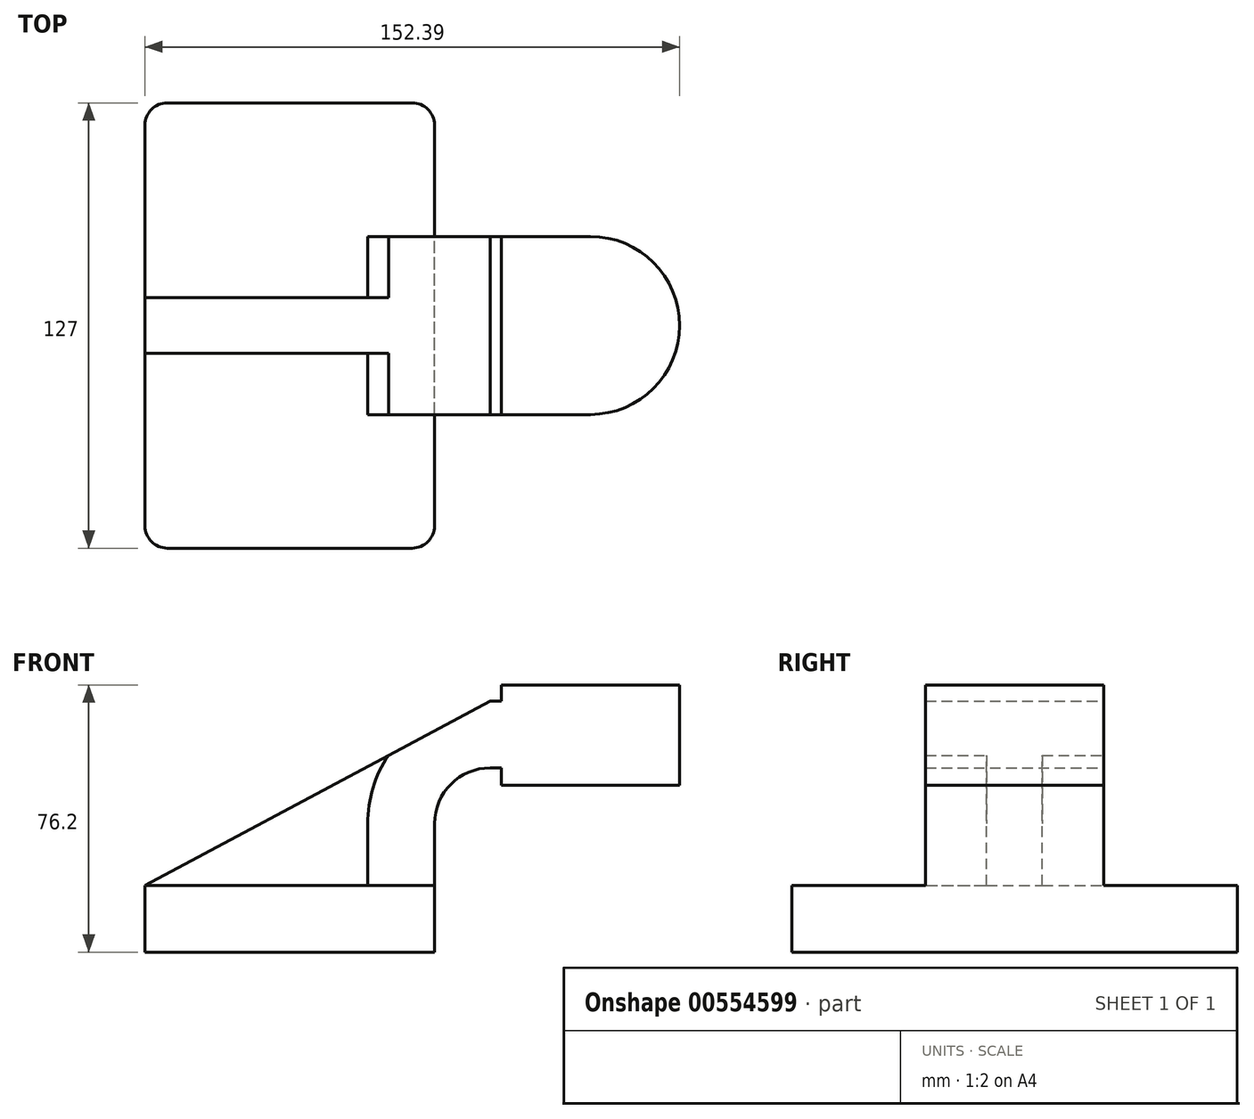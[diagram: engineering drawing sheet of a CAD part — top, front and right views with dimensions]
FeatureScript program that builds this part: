
annotation { "Feature Type Name" : "Feature", "Feature Type Description" : "" }
export const myFeature = defineFeature(function(context is Context, id is Id, definition is map)
    precondition{}
    {
        {
            var Q0;
            Q0=qCreatedBy(makeId("Front.planeOp"),FACE);
            var sketch = newSketch(context, id + "F0", { "sketchPlane" : qUnion([Q0])});
            skLineSegment(sketch, "E0.bottom", {"start": v(-41.28, 9.52) * mm, "end": v(41.27, 9.53) * mm});
            skLineSegment(sketch, "E0.top", {"start": v(-41.28, -9.53) * mm, "end": v(41.28, -9.53) * mm});
            skLineSegment(sketch, "E0.left", {"start": v(-41.28, 9.52) * mm, "end": v(-41.27, -9.53) * mm});
            skLineSegment(sketch, "E0.right", {"start": v(41.28, 9.53) * mm, "end": v(41.28, -9.52) * mm});
            skPoint(sketch, "E0.middle", {"position": v(0, 0) * mm});
            skLineSegment(sketch, "E1.bottom", {"start": v(60.32, 66.67) * mm, "end": v(111.12, 66.67) * mm});
            skLineSegment(sketch, "E1.top", {"start": v(60.33, 38.1) * mm, "end": v(111.12, 38.1) * mm});
            skLineSegment(sketch, "E1.left", {"start": v(60.32, 66.67) * mm, "end": v(60.33, 38.1) * mm});
            skLineSegment(sketch, "E1.right", {"start": v(111.12, 66.67) * mm, "end": v(111.12, 38.1) * mm});
            skPoint(sketch, "E1.middle", {"position": v(85.72, 52.39) * mm});
            skLineSegment(sketch, "E2", {"start": v(41.27, 9.53) * mm, "end": v(41.27, 27.13) * mm});
            skArc(sketch, "E3", {"start": v(41.27, 27.13) * mm, "mid": v(45.92, 38.35) * mm, "end": v(57.15, 43) * mm});
            skLineSegment(sketch, "E4", {"start": v(57.15, 43) * mm, "end": v(76.83, 43) * mm});
            skLineSegment(sketch, "E5.0", {"start": v(57.15, 62.05) * mm, "end": v(76.83, 62.05) * mm});
            skArc(sketch, "E5.1", {"start": v(22.22, 27.13) * mm, "mid": v(32.45, 51.82) * mm, "end": v(57.15, 62.05) * mm});
            skLineSegment(sketch, "E5.2", {"start": v(22.22, 9.53) * mm, "end": v(22.22, 27.13) * mm});
            skLineSegment(sketch, "E6", {"start": v(85.72, 38.1) * mm, "end": v(85.72, 66.67) * mm});
            skFitSpline(sketch, "E7", {"points": [v(-41.28, 9.52) * mm, v(57.15, 62.05) * mm], "startDerivative": vector(98.43, 52.53) * mm, "endDerivative": vector(98.43, 52.53) * mm});
            skSolve(sketch);
        }
        {
            var Q0;
            Q0=makeQuery(id+"F0.imprint","IMPRINT",FACE,{"disambiguationData":[TD([[makeQuery(id+"F0.imprint","IMPRINT",EDGE,{"derivedFrom":sQuery(id+"F0.wireOp",EDGE,"E0.top")}),1.0]])]});
            extrude(context, id + "F1", {"entities" : qUnion([Q0]), "endBound" : BoundingType.SYMMETRIC, "depth" : 127 * mm, "offsetDistance" : 25.4 * mm});
        }
        {
            var Q0;
            {var subQ1=sQuery(id+"F0.wireOp",EDGE,"E2");Q0=makeQuery(id+"F0.imprint","IMPRINT",FACE,{"disambiguationData":[TD([[makeQuery(id+"F0.imprint","IMPRINT",EDGE,{"derivedFrom":subQ1}),1.0]])]});}
            var Q1;
            {var subQ4=sQuery(id+"F0.wireOp",EDGE,"E6");Q1=makeQuery(id+"F0.imprint","IMPRINT",FACE,{"disambiguationData":[TD([[makeQuery(id+"F0.imprint","IMPRINT",EDGE,{"derivedFrom":subQ4}),1.0]])]});}
            extrude(context, id + "F2", {"entities" : qUnion([Q0, Q1]), "operationType" : NewBodyOperationType.ADD, "endBound" : BoundingType.SYMMETRIC, "depth" : 50.8 * mm, "offsetDistance" : 25.4 * mm});
        }
        {
            var Q0;
            {var subQ3=sQuery(id+"F0.wireOp",EDGE,"E5.2");Q0=makeQuery(id+"F0.imprint","IMPRINT",FACE,{"disambiguationData":[TD([[makeQuery(id+"F0.imprint","IMPRINT",EDGE,{"derivedFrom":subQ3}),1.0]])]});}
            extrude(context, id + "F3", {"entities" : qUnion([Q0]), "operationType" : NewBodyOperationType.ADD, "endBound" : BoundingType.SYMMETRIC, "depth" : 15.88 * mm, "offsetDistance" : 25.4 * mm});
        }
        {
            var Q0;
            {var subQ0=sQuery(id+"F0.wireOp",EDGE,"E1.right");Q0=makeQuery(id+"F0.imprint","IMPRINT",FACE,{"disambiguationData":[TD([[makeQuery(id+"F0.imprint","IMPRINT",EDGE,{"derivedFrom":subQ0}),-1.0]])]});}
            var Q1;
            Q1=sQuery(id+"F0.wireOp",EDGE,"E6");
            revolve(context, id + "F4", {"operationType" : NewBodyOperationType.ADD, "entities" : qUnion([Q0]), "axis" : qUnion([Q1]), "revolveType" : RevolveType.FULL});
        }
        {
            var Q0;
            Q0=makeQuery(id+"F1.opExtrude","CAP_EDGE",EDGE,{"disambiguationData":[OSD([sQuery(id+"F0.wireOp",EDGE,"E0.right")])],"isStart":false});
            var Q1;
            Q1=makeQuery(id+"F1.opExtrude","CAP_EDGE",EDGE,{"disambiguationData":[OSD([sQuery(id+"F0.wireOp",EDGE,"E0.left")])],"isStart":false});
            var Q2;
            Q2=makeQuery(id+"F1.opExtrude","CAP_EDGE",EDGE,{"disambiguationData":[OSD([sQuery(id+"F0.wireOp",EDGE,"E0.left")])],"isStart":true});
            var Q3;
            Q3=makeQuery(id+"F1.opExtrude","CAP_EDGE",EDGE,{"disambiguationData":[OSD([sQuery(id+"F0.wireOp",EDGE,"E0.right")])],"isStart":true});
            fillet(context, id + "F5", {"entities" : qUnion([Q0, Q1, Q2, Q3]), "radius" : 6.35 * mm, "tangentPropagation" : true, "allowEdgeOverflow" : false});
        }
    });
